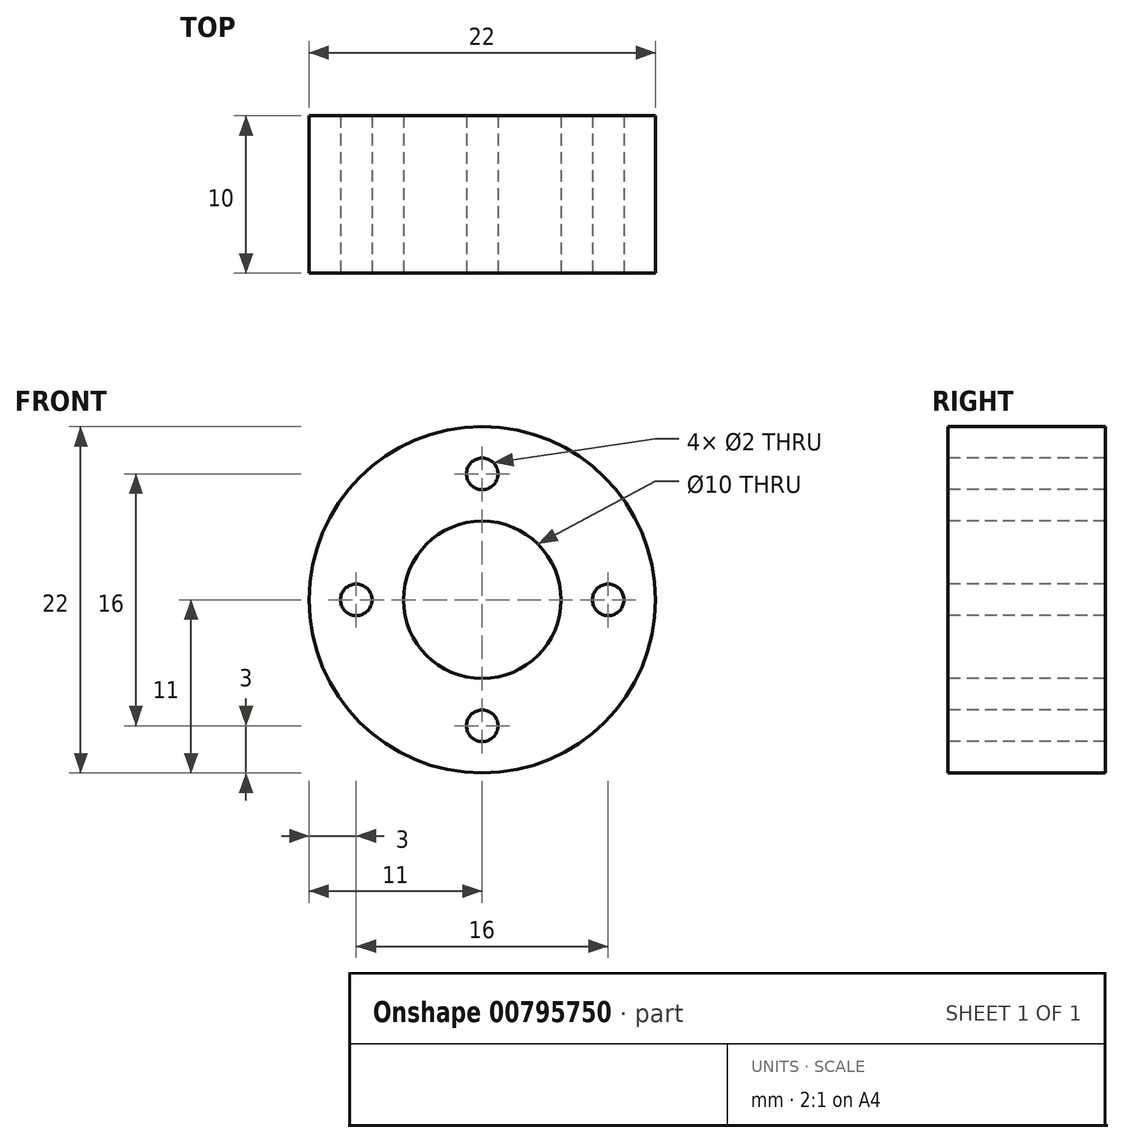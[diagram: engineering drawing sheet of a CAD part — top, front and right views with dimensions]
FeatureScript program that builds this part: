
annotation { "Feature Type Name" : "Feature", "Feature Type Description" : "" }
export const myFeature = defineFeature(function(context is Context, id is Id, definition is map)
    precondition{}
    {
        {
            var Q0;
            Q0=qCreatedBy(makeId("Front.planeOp"),FACE);
            var sketch = newSketch(context, id + "F0", { "sketchPlane" : qUnion([Q0])});
            skCircle(sketch, "E0", {"center": v(0, 0) * mm, "radius": 11 * mm});
            skSolve(sketch);
        }
        {
            var Q0;
            Q0=makeQuery(id+"F0.imprint","IMPRINT",FACE,{"disambiguationData":[TD([[makeQuery(id+"F0.imprint","IMPRINT",EDGE,{"derivedFrom":sQuery(id+"F0.wireOp",EDGE,"E0")}),1.0]])]});
            extrude(context, id + "F1", {"entities" : qUnion([Q0]), "depth" : 10 * mm, "offsetDistance" : 25 * mm});
        }
        {
            var Q0;
            Q0=makeQuery(id+"F1.opExtrude","CAP_FACE",FACE,{"disambiguationData":[OSD([sQuery(id+"F0.wireOp",EDGE,"E0")])],"isStart":false});
            var sketch = newSketch(context, id + "F2", { "sketchPlane" : qUnion([Q0])});
            skCircle(sketch, "E1", {"center": v(0, 0) * mm, "radius": 5 * mm});
            skSolve(sketch);
        }
        {
            var Q0;
            Q0=makeQuery(id+"F2.imprint","IMPRINT",FACE,{"disambiguationData":[TD([[makeQuery(id+"F2.imprint","IMPRINT",EDGE,{"derivedFrom":sQuery(id+"F2.wireOp",EDGE,"E1")}),1.0]])]});
            extrude(context, id + "F3", {"entities" : qUnion([Q0]), "operationType" : NewBodyOperationType.REMOVE, "oppositeDirection" : true, "depth" : 25 * mm, "offsetDistance" : 25 * mm});
        }
        {
            var Q0;
            Q0=makeQuery(id+"F1.opExtrude","CAP_FACE",FACE,{"disambiguationData":[OSD([sQuery(id+"F0.wireOp",EDGE,"E0")])],"isStart":false});
            var sketch = newSketch(context, id + "F4", { "sketchPlane" : qUnion([Q0])});
            skCircle(sketch, "E2", {"center": v(0, 0) * mm, "radius": 8 * mm, "construction": true});
            skCircle(sketch, "E3", {"center": v(-8, 0) * mm, "radius": 1 * mm});
            skCircle(sketch, "E4.1.0", {"center": v(0, -8) * mm, "radius": 1 * mm});
            skCircle(sketch, "E4.2.0", {"center": v(8, 0) * mm, "radius": 1 * mm});
            skCircle(sketch, "E4.3.0", {"center": v(0, 8) * mm, "radius": 1 * mm});
            skSolve(sketch);
        }
        {
            var Q0;
            Q0=makeQuery(id+"F4.imprint","IMPRINT",FACE,{"disambiguationData":[TD([[makeQuery(id+"F4.imprint","IMPRINT",EDGE,{"derivedFrom":sQuery(id+"F4.wireOp",EDGE,"E3")}),1.0]])]});
            var Q1;
            Q1=makeQuery(id+"F4.imprint","IMPRINT",FACE,{"disambiguationData":[TD([[makeQuery(id+"F4.imprint","IMPRINT",EDGE,{"derivedFrom":sQuery(id+"F4.wireOp",EDGE,"E4.3.0")}),1.0]])]});
            var Q2;
            Q2=makeQuery(id+"F4.imprint","IMPRINT",FACE,{"disambiguationData":[TD([[makeQuery(id+"F4.imprint","IMPRINT",EDGE,{"derivedFrom":sQuery(id+"F4.wireOp",EDGE,"E4.2.0")}),1.0]])]});
            var Q3;
            Q3=makeQuery(id+"F4.imprint","IMPRINT",FACE,{"disambiguationData":[TD([[makeQuery(id+"F4.imprint","IMPRINT",EDGE,{"derivedFrom":sQuery(id+"F4.wireOp",EDGE,"E4.1.0")}),1.0]])]});
            extrude(context, id + "F5", {"entities" : qUnion([Q0, Q1, Q2, Q3]), "operationType" : NewBodyOperationType.REMOVE, "oppositeDirection" : true, "depth" : 25 * mm, "offsetDistance" : 25 * mm});
        }
    });
